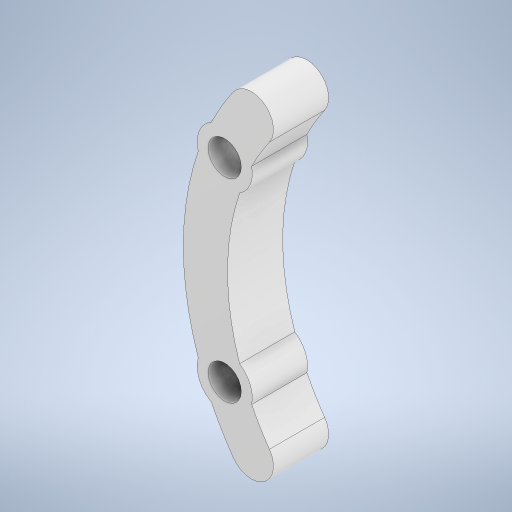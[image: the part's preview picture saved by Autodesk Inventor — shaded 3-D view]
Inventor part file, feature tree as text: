
AUTODESK INVENTOR PART (.ipt)
format: ipt  version: 2024.3 (Build 283343000, 343)  size: 297,984 bytes
history: native  units: mm
features: extrude x2, sketch x2, other x1, fillet x1
ambient origin geometry x8: Origin, YZ Plane, XZ Plane, XY Plane, X Axis, Y Axis, Z Axis, Center Point
bodies: Body1 (feature_tree)
feature tree (6):
  other  "ソリッド1"
  extrude  "押し出し1"  Depth=92.0mm
  fillet  "フィレット1"  Radius=100.0mm
  extrude  "押し出し2"  Depth=84.0mm
  sketch  "スケッチ1"
  sketch  "スケッチ2"
